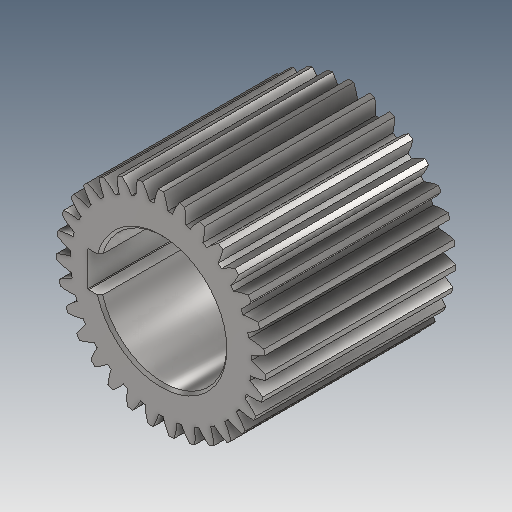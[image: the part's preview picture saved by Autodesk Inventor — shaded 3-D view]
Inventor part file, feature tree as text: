
AUTODESK INVENTOR PART (.ipt)
format: ipt  version: 2025 (Build 290162000, 162)  size: 430,080 bytes
history: native  units: mm (DEFAULTED — no unit token found)
features: other x5, plane x3, extrude x2, sketch x2, chamfer x1
ambient origin geometry x8: Origin, YZ Plane, XZ Plane, XY Plane, X Axis, Y Axis, Z Axis, Center Point
bodies: Solid1 (feature_tree)
feature tree (13):
  other  "{BB8FE430-83BF-418D-8DF9-9B323D3DB9B9}"
  extrude  "Extrusion1"  Depth=75.0mm TaperAngle=0.0deg
  plane  "Work Plane2"
  plane  "Work Plane8"
  plane  "Work Plane9"
  other  "正齿轮"
  extrude  "拉伸2"  Depth=10.0mm TaperAngle=0.0deg
  chamfer  "倒角1"  Distance=166.25mm
  other  "键槽3"
  sketch  "Sketch1"  dims[d0=82.5mm d1=75.0mm d2=0.0mm]
  other  "Srf1"
  sketch  "草图3"  dims[d3=77.5mm d4=10.0mm d5=0.0mm d16=166.25mm d17=0.0mm d34=1.013417mm d39=0.0mm d41=0.0mm d43=166.25mm d46=166.25mm d47=0.0mm d48=0.0mm d49=50.0mm d50=10.0mm d51=0.0mm d52=1.0mm d53=2.0mm d54=45.0deg d55=14.0mm d56=9.0mm]
  other  "轮毂键槽"
